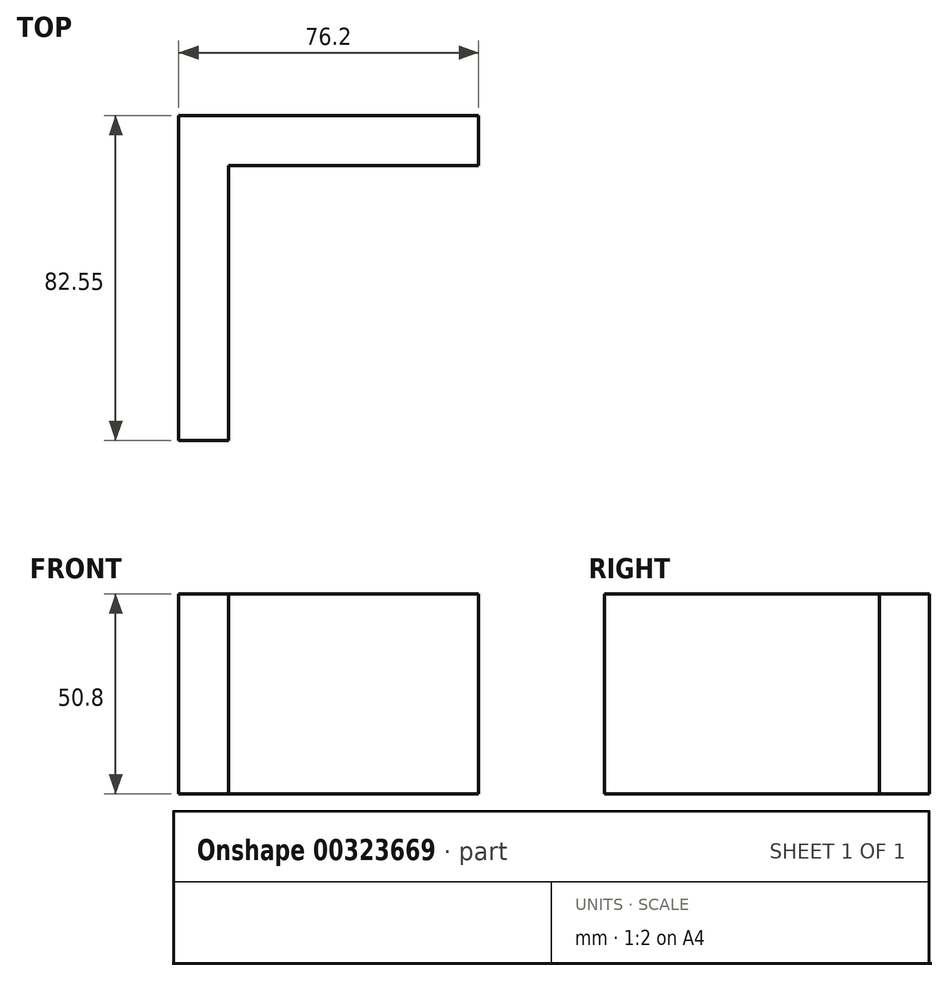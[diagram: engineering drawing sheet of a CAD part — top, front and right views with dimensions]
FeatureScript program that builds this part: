
annotation { "Feature Type Name" : "Feature", "Feature Type Description" : "" }
export const myFeature = defineFeature(function(context is Context, id is Id, definition is map)
    precondition{}
    {
        {
            var Q0;
            Q0=qCreatedBy(makeId("Top.planeOp"),FACE);
            var sketch = newSketch(context, id + "F0", { "sketchPlane" : qUnion([Q0])});
            skLineSegment(sketch, "E0", {"start": v(0, 0) * mm, "end": v(0, -82.55) * mm});
            skLineSegment(sketch, "E1", {"start": v(0, -82.55) * mm, "end": v(12.7, -82.55) * mm});
            skLineSegment(sketch, "E2", {"start": v(12.7, -82.55) * mm, "end": v(12.7, -12.7) * mm});
            skLineSegment(sketch, "E3", {"start": v(12.7, -12.7) * mm, "end": v(76.2, -12.7) * mm});
            skLineSegment(sketch, "E4", {"start": v(76.2, -12.7) * mm, "end": v(76.2, 0) * mm});
            skLineSegment(sketch, "E5", {"start": v(76.2, 0) * mm, "end": v(0, 0) * mm});
            skSolve(sketch);
        }
        {
            var Q0;
            Q0=makeQuery(id+"F0.imprint","IMPRINT",FACE,{"disambiguationData":[TD([[makeQuery(id+"F0.imprint","IMPRINT",EDGE,{"derivedFrom":sQuery(id+"F0.wireOp",EDGE,"E0")}),1.0]])]});
            extrude(context, id + "F1", {"entities" : qUnion([Q0]), "depth" : 50.8 * mm});
        }
    });
